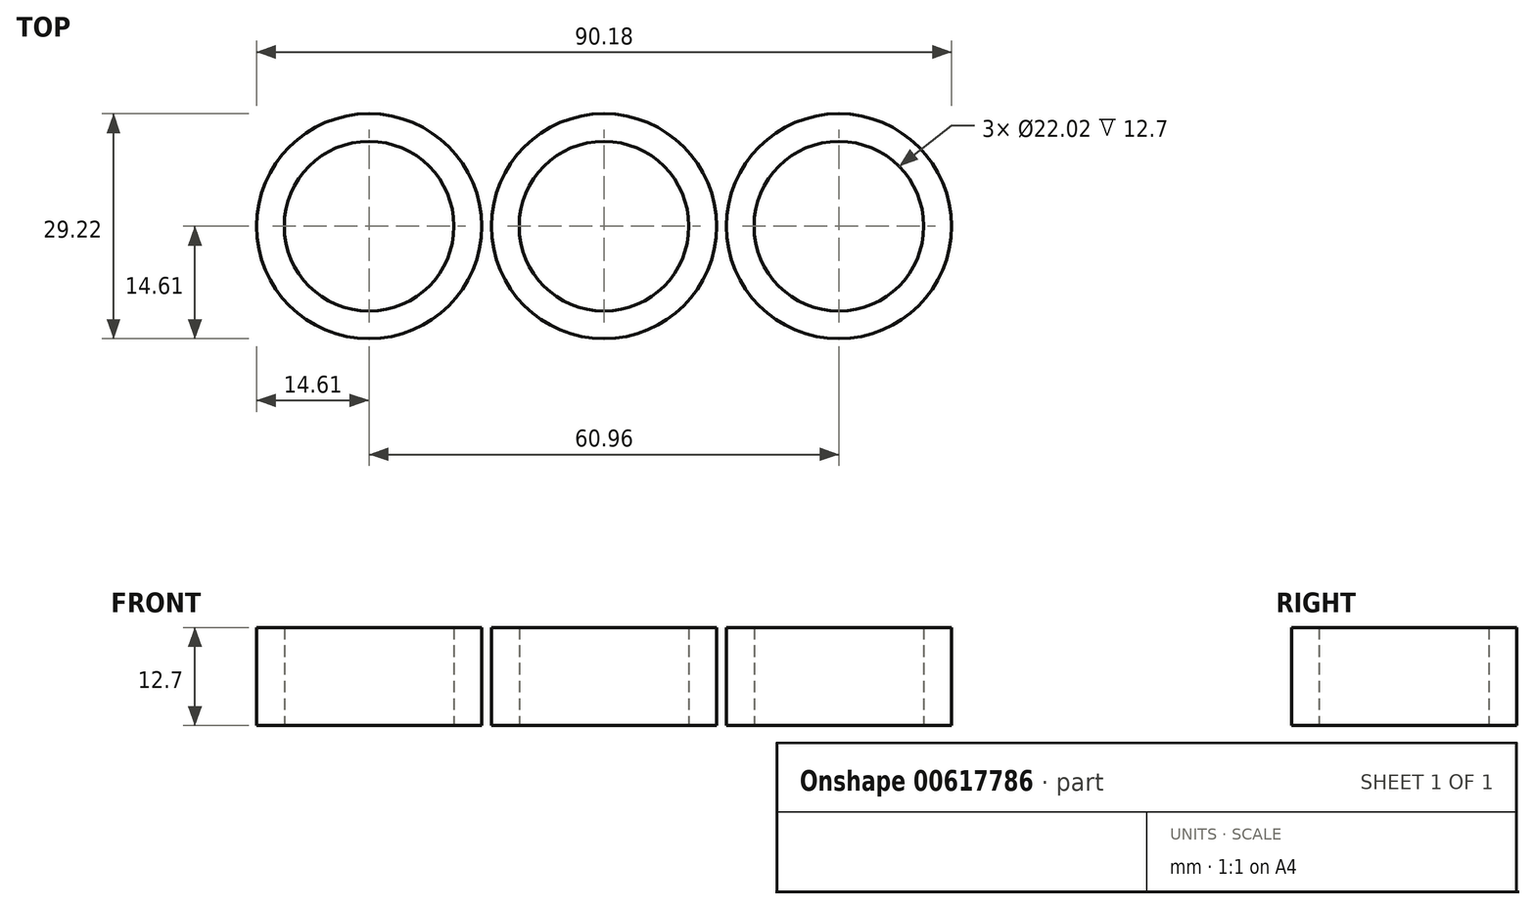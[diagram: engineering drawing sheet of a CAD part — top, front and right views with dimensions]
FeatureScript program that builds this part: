
annotation { "Feature Type Name" : "Feature", "Feature Type Description" : "" }
export const myFeature = defineFeature(function(context is Context, id is Id, definition is map)
    precondition{}
    {
        {
            var Q0;
            Q0=qCreatedBy(makeId("Top.planeOp"),FACE);
            var sketch = newSketch(context, id + "F0", { "sketchPlane" : qUnion([Q0])});
            skCircle(sketch, "E0", {"center": v(0, 0) * mm, "radius": 11.01 * mm});
            skLineSegment(sketch, "E1", {"start": v(0, 0) * mm, "end": v(-30.48, 0) * mm});
            skCircle(sketch, "E2", {"center": v(-30.48, 0) * mm, "radius": 11.01 * mm});
            skLineSegment(sketch, "E3", {"start": v(0, 0) * mm, "end": v(30.48, 0) * mm});
            skCircle(sketch, "E4", {"center": v(30.48, 0) * mm, "radius": 11.01 * mm});
            skCircle(sketch, "E5", {"center": v(-30.48, 0) * mm, "radius": 14.6 * mm});
            skCircle(sketch, "E6", {"center": v(0, 0) * mm, "radius": 14.6 * mm});
            skCircle(sketch, "E7", {"center": v(30.48, 0) * mm, "radius": 14.6 * mm});
            skLineSegment(sketch, "E8", {"start": v(-30.48, 14.6) * mm, "end": v(30.48, 14.6) * mm});
            skLineSegment(sketch, "E9", {"start": v(-30.48, -14.6) * mm, "end": v(30.48, -14.6) * mm});
            skSolve(sketch);
        }
        {
            var Q0;
            Q0=makeQuery(id+"F0.imprint","IMPRINT",FACE,{"disambiguationData":[TD([[makeQuery(id+"F0.imprint","IMPRINT",EDGE,{"derivedFrom":sQuery(id+"F0.wireOp",EDGE,"E2")}),-1.0]])]});
            var Q1;
            {var subQ2=sQuery(id+"F0.wireOp",EDGE,"E1");var subQ5=sQuery(id+"F0.wireOp",EDGE,"E0");var subQ8=makeQuery(id+"F0.imprint","INTERSECT",VERTEX,{"derivedFrom":[subQ5,subQ2]});Q1=makeQuery(id+"F0.imprint","IMPRINT",FACE,{"disambiguationData":[TD([[makeQuery(id+"F0.imprint","IMPRINT",EDGE,{"disambiguationData":[TD([[subQ8,-1.0]])],"derivedFrom":subQ5}),-1.0]])]});}
            var Q2;
            {var subQ1=sQuery(id+"F0.wireOp",EDGE,"E0");var subQ6=sQuery(id+"F0.wireOp",EDGE,"E1");var subQ7=makeQuery(id+"F0.imprint","INTERSECT",VERTEX,{"derivedFrom":[subQ1,subQ6]});Q2=makeQuery(id+"F0.imprint","IMPRINT",FACE,{"disambiguationData":[TD([[makeQuery(id+"F0.imprint","IMPRINT",EDGE,{"disambiguationData":[TD([[subQ7,1.0]])],"derivedFrom":subQ1}),-1.0]])]});}
            var Q3;
            Q3=makeQuery(id+"F0.imprint","IMPRINT",FACE,{"disambiguationData":[TD([[makeQuery(id+"F0.imprint","IMPRINT",EDGE,{"derivedFrom":sQuery(id+"F0.wireOp",EDGE,"E4")}),-1.0]])]});
            extrude(context, id + "F1", {"entities" : qUnion([Q0, Q1, Q2, Q3]), "depth" : 12.7 * mm, "offsetDistance" : 25.4 * mm});
        }
    });
